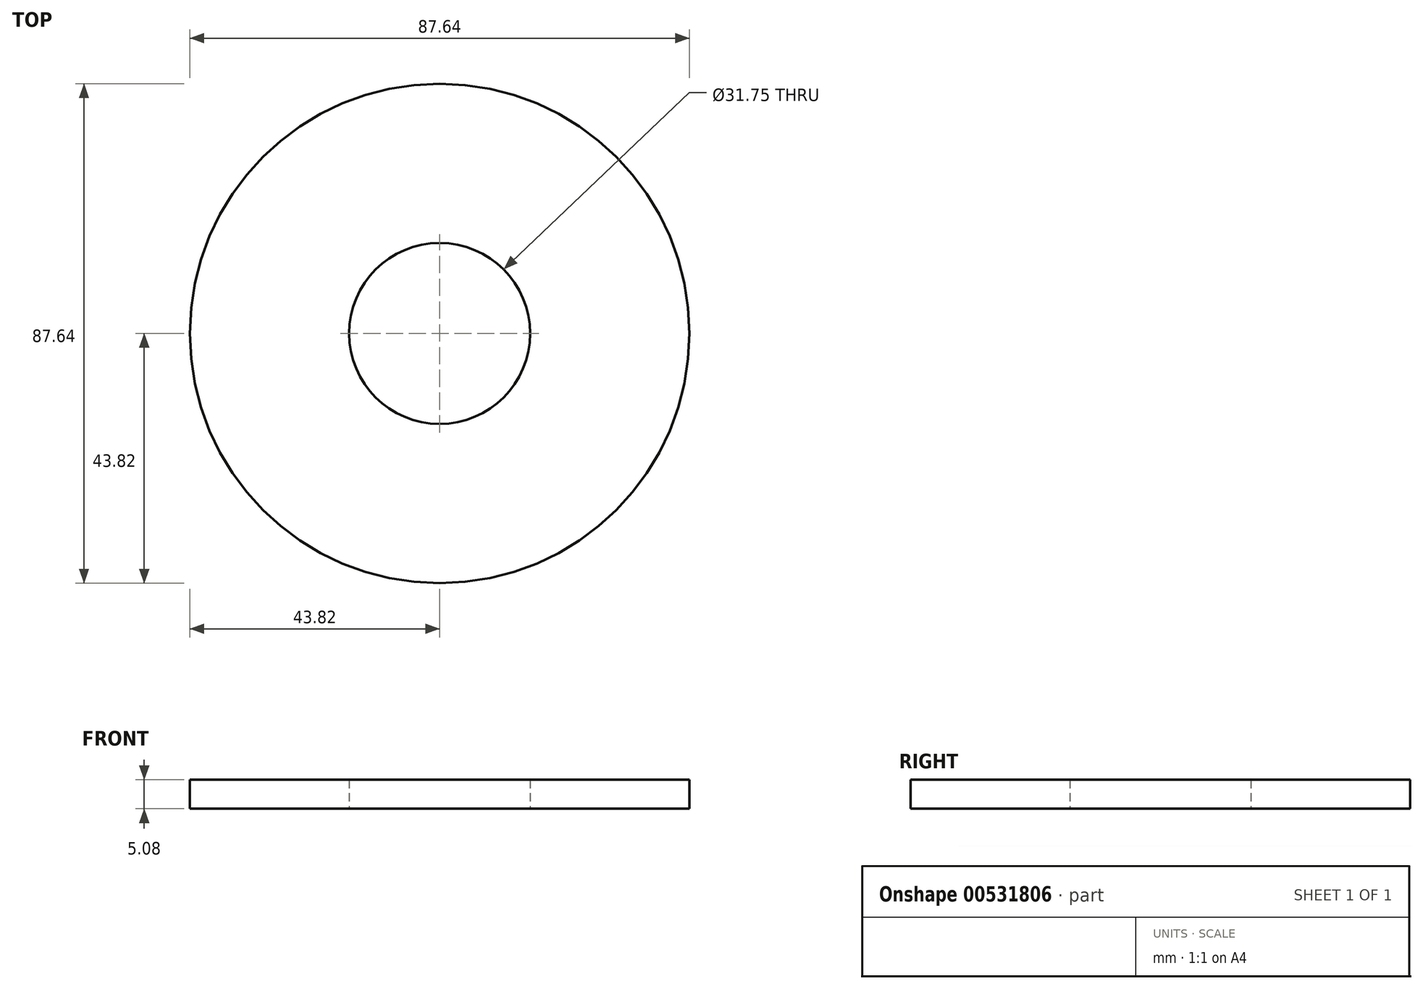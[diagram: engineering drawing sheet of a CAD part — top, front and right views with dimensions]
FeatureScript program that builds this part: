
annotation { "Feature Type Name" : "Feature", "Feature Type Description" : "" }
export const myFeature = defineFeature(function(context is Context, id is Id, definition is map)
    precondition{}
    {
        {
            var Q0;
            Q0=qCreatedBy(makeId("Top.planeOp"),FACE);
            var sketch = newSketch(context, id + "F0", { "sketchPlane" : qUnion([Q0])});
            skCircle(sketch, "E0", {"center": v(0, 0) * mm, "radius": 43.82 * mm});
            skSolve(sketch);
        }
        {
            var Q0;
            Q0 = qSketchRegion(id + "F0", true);
            extrude(context, id + "F1", {"entities" : qUnion([Q0]), "depth" : 5.08 * mm, "offsetDistance" : 25.4 * mm});
        }
        {
            var Q0;
            Q0=qCreatedBy(makeId("Top.planeOp"),FACE);
            var sketch = newSketch(context, id + "F2", { "sketchPlane" : qUnion([Q0])});
            skCircle(sketch, "E1", {"center": v(0, 0) * mm, "radius": 15.88 * mm});
            skSolve(sketch);
        }
        {
            var Q0;
            Q0 = qSketchRegion(id + "F2", true);
            extrude(context, id + "F3", {"entities" : qUnion([Q0]), "operationType" : NewBodyOperationType.REMOVE, "endBound" : BoundingType.THROUGH_ALL, "depth" : 25.4 * mm, "offsetDistance" : 25.4 * mm});
        }
    });
